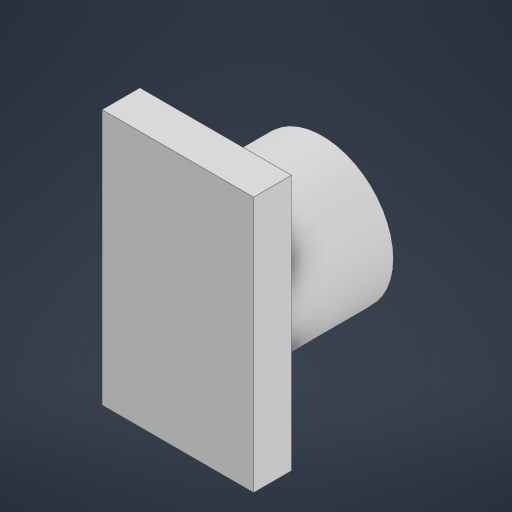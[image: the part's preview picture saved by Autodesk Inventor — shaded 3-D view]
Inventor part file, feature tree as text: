
AUTODESK INVENTOR PART (.ipt)
format: ipt  version: 2023 (Build 270158000, 158)  size: 183,808 bytes
history: native  units: in
note: dims shown in document units (in); Inventor stores cm internally (conversion verified against a paired STEP export)
features: extrude x2, sketch x1, chamfer x1
ambient origin geometry x8: Origin, YZ Plane, XZ Plane, XY Plane, X Axis, Y Axis, Z Axis, Center Point
bodies: Solid1 (feature_tree)
feature tree (4):
  sketch  "Sketch1"  dims[d0=0.126in d1=0.2126in d2=0.0315in d3=0.0in d4=0.0984in d5=0.0in d6=0.0315in d7=0.0098in d8=15.0deg d9=0.1181in d10=0.0157in d11=0.0197in d12=0.0344in d13=0.0344in]
  extrude  "Extrusion1"  Depth=0.2126in
  extrude  "Extrusion2"  Depth=0.0315in TaperAngle=0.0deg
  chamfer  "Chamfer1"  Distance=0.0984in
